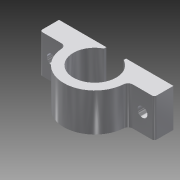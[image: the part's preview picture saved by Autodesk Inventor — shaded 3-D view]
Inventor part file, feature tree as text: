
AUTODESK INVENTOR PART (.ipt)
format: ipt  version: 2013 (Build 170138000, 138)  size: 153,088 bytes
history: native  units: in
note: dims shown in document units (in); Inventor stores cm internally (conversion verified against a paired STEP export)
features: sketch x2, extrude x2, projected_geometry x2, fillet x1
ambient origin geometry x8: Origin, YZ Plane, XZ Plane, XY Plane, X Axis, Y Axis, Z Axis, Center Point
bodies: Solid1 (feature_tree)
feature tree (7):
  sketch  "Sketch1"  dims[d0=1.5in d1=1.375in d3=1.0in d4=0.0in]
  extrude  "Extrusion1"  Depth=1.375in
  fillet  "Fillet1"  Radius=1.0in
  extrude  "Extrusion3"  Depth=0.75in
  sketch  "Sketch5"  dims[d9=0.5in d10=0.75in d11=0.75in d12=0.5in d14=0.125in d15=0.26in d16=0.26in d17=0.25in d18=0.0in d21=1.125in d22=0.5625in d23=0.0625in d24=1.1875in d25=1.1875in d26=2.375in d34=0.0625in]
  projected_geometry  "Projected Loop1"
  projected_geometry  "Projected Loop2"
